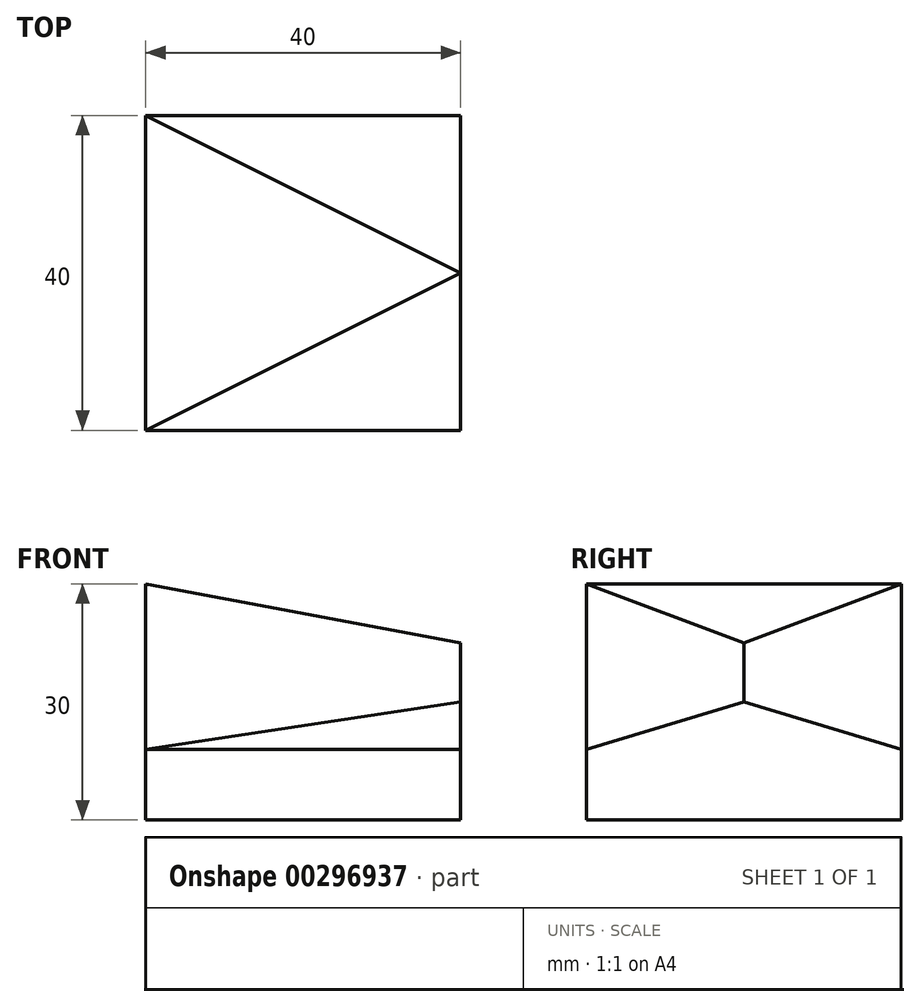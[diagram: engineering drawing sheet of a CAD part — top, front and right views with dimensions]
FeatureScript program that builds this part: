
annotation { "Feature Type Name" : "Feature", "Feature Type Description" : "" }
export const myFeature = defineFeature(function(context is Context, id is Id, definition is map)
    precondition{}
    {
        {
            var Q0;
            Q0=qCreatedBy(makeId("Top.planeOp"),FACE);
            var sketch = newSketch(context, id + "F0", { "sketchPlane" : qUnion([Q0])});
            skLineSegment(sketch, "E0.bottom", {"start": v(0, 0) * mm, "end": v(40, 0) * mm});
            skLineSegment(sketch, "E0.top", {"start": v(0, 40) * mm, "end": v(40, 40) * mm});
            skLineSegment(sketch, "E0.left", {"start": v(0, 0) * mm, "end": v(0, 40) * mm});
            skLineSegment(sketch, "E0.right", {"start": v(40, 0) * mm, "end": v(40, 40) * mm});
            skLineSegment(sketch, "E1", {"start": v(40, 20) * mm, "end": v(0, 0) * mm});
            skLineSegment(sketch, "E2", {"start": v(40, 20) * mm, "end": v(0, 40) * mm});
            skSolve(sketch);
        }
        {
            var Q0;
            Q0=qSketchRegion(id+"F0",true);
            extrude(context, id + "F1", {"entities" : qUnion([Q0]), "depth" : 15 * mm});
        }
        {
            var Q0;
            Q0=makeQuery(id+"F1.opExtrude","SWEPT_FACE",FACE,{"disambiguationData":[OSD([sQuery(id+"F0.wireOp",EDGE,"E0.right")])]});
            var sketch = newSketch(context, id + "F2", { "sketchPlane" : qUnion([Q0])});
            skLineSegment(sketch, "E3", {"start": v(20, 15) * mm, "end": v(0, 9) * mm});
            skLineSegment(sketch, "E4", {"start": v(20, 15) * mm, "end": v(40, 9) * mm});
            skSolve(sketch);
        }
        {
            var Q0;
            Q0 = qSketchRegion(id + "F2", true);
            var Q1;
            {var subQ0=sQuery(id+"F2.wireOp",EDGE,"E3");Q1=makeQuery(id+"F2.imprint","IMPRINT",FACE,{"disambiguationData":[TD([[makeQuery(id+"F2.imprint","IMPRINT",EDGE,{"derivedFrom":subQ0}),-1.0]])]});}
            var Q2;
            {var subQ0=sQuery(id+"F2.wireOp",EDGE,"E4");Q2=makeQuery(id+"F2.imprint","IMPRINT",FACE,{"disambiguationData":[TD([[makeQuery(id+"F2.imprint","IMPRINT",EDGE,{"derivedFrom":subQ0}),1.0]])]});}
            extrude(context, id + "F3", {"entities" : qUnion([Q0, Q1, Q2]), "operationType" : NewBodyOperationType.REMOVE, "endBound" : BoundingType.THROUGH_ALL, "oppositeDirection" : true, "depth" : 25 * mm});
        }
        {
            var Q0;
            Q0=makeQuery(id+"F0.imprint","IMPRINT",FACE,{"disambiguationData":[TD([[makeQuery(id+"F0.imprint","IMPRINT",EDGE,{"derivedFrom":sQuery(id+"F0.wireOp",EDGE,"E0.left")}),-1.0]])]});
            extrude(context, id + "F4", {"entities" : qUnion([Q0]), "operationType" : NewBodyOperationType.ADD, "depth" : 30 * mm});
        }
        {
            var Q0;
            Q0=makeQuery(id+"F4.opExtrude","SWEPT_EDGE",EDGE,{"disambiguationData":[OSD([sQuery(id+"F0.wireOp",EDGE,"E0.right"),sQuery(id+"F0.wireOp",EDGE,"E1"),sQuery(id+"F0.wireOp",EDGE,"E2")])]});
            cPoint(context, id + "F5", {"entities" : qUnion([Q0]), "parameter" : 0.5});
        }
        {
            var Q0;
            Q0=makeQuery(id+"F4.opExtrude","CAP_VERTEX",VERTEX,{"disambiguationData":[OSD([sQuery(id+"F0.wireOp",EDGE,"E0.top"),sQuery(id+"F0.wireOp",EDGE,"E0.left"),sQuery(id+"F0.wireOp",EDGE,"E2")])],"isStart":false});
            var Q1;
            Q1=makeQuery(id+"F4.opExtrude","CAP_VERTEX",VERTEX,{"disambiguationData":[OSD([sQuery(id+"F0.wireOp",EDGE,"E0.bottom"),sQuery(id+"F0.wireOp",EDGE,"E0.left"),sQuery(id+"F0.wireOp",EDGE,"E1")])],"isStart":false});
            var Q2;
            Q2=qCreatedBy(id+"F5",VERTEX);
            cPlane(context, id + "F6", {"entities" : qUnion([Q0, Q1, Q2]), "cplaneType" : CPlaneType.THREE_POINT, "offset" : 25 * mm, "width" : 150 * mm, "height" : 150 * mm});
        }
        {
            var Q0;
            Q0=qCreatedBy(id+"F6.planeOp",FACE);
            var sketch = newSketch(context, id + "F7", { "sketchPlane" : qUnion([Q0])});
            skPoint(sketch, "E5.0", {"position": v(-5.53, 0) * mm});
            skPoint(sketch, "E6.0", {"position": v(-5.53, -40) * mm});
            skPoint(sketch, "E7.0", {"position": v(35.17, -20) * mm});
            skLineSegment(sketch, "E8", {"start": v(-5.53, 0) * mm, "end": v(-5.53, -40) * mm});
            skLineSegment(sketch, "E9", {"start": v(-5.53, -40) * mm, "end": v(35.17, -20) * mm});
            skLineSegment(sketch, "E10", {"start": v(35.17, -20) * mm, "end": v(-5.53, 0) * mm});
            skSolve(sketch);
        }
        {
            var Q0;
            Q0=qSketchRegion(id+"F7",true);
            extrude(context, id + "F8", {"entities" : qUnion([Q0]), "operationType" : NewBodyOperationType.REMOVE, "endBound" : BoundingType.THROUGH_ALL, "oppositeDirection" : true, "depth" : 25 * mm});
        }
    });
